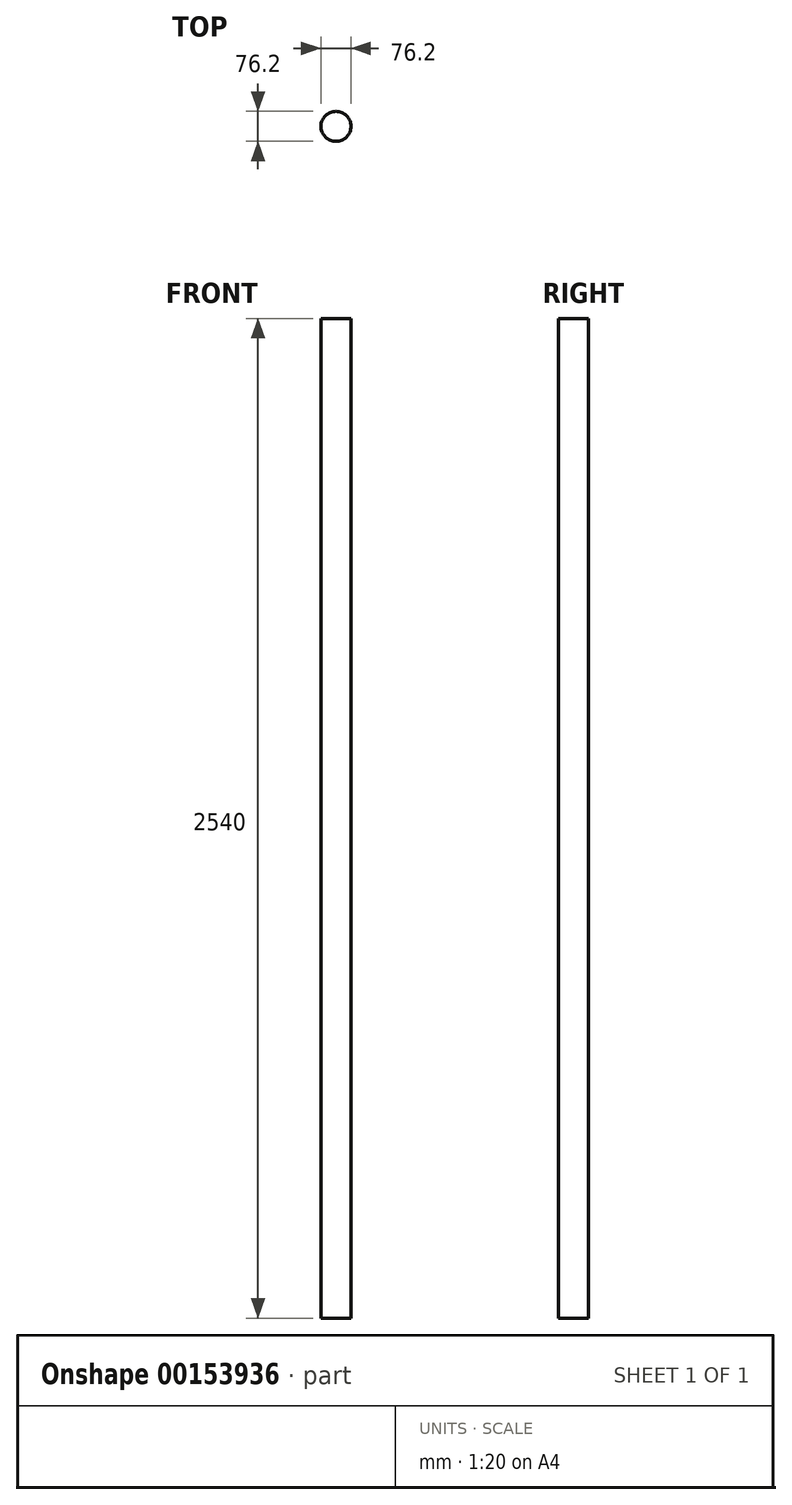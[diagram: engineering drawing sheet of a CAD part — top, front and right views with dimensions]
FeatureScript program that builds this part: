
annotation { "Feature Type Name" : "Feature", "Feature Type Description" : "" }
export const myFeature = defineFeature(function(context is Context, id is Id, definition is map)
    precondition{}
    {
        {
            var Q0;
            Q0=qCreatedBy(makeId("Top.planeOp"),FACE);
            var sketch = newSketch(context, id + "F0", { "sketchPlane" : qUnion([Q0])});
            skCircle(sketch, "E0", {"center": v(0, 0) * mm, "radius": 38.1 * mm});
            skSolve(sketch);
        }
        {
            var Q0;
            Q0 = qSketchRegion(id + "F0", true);
            extrude(context, id + "F1", {"entities" : qUnion([Q0]), "oppositeDirection" : true, "depth" : 2540 * mm});
        }
    });
